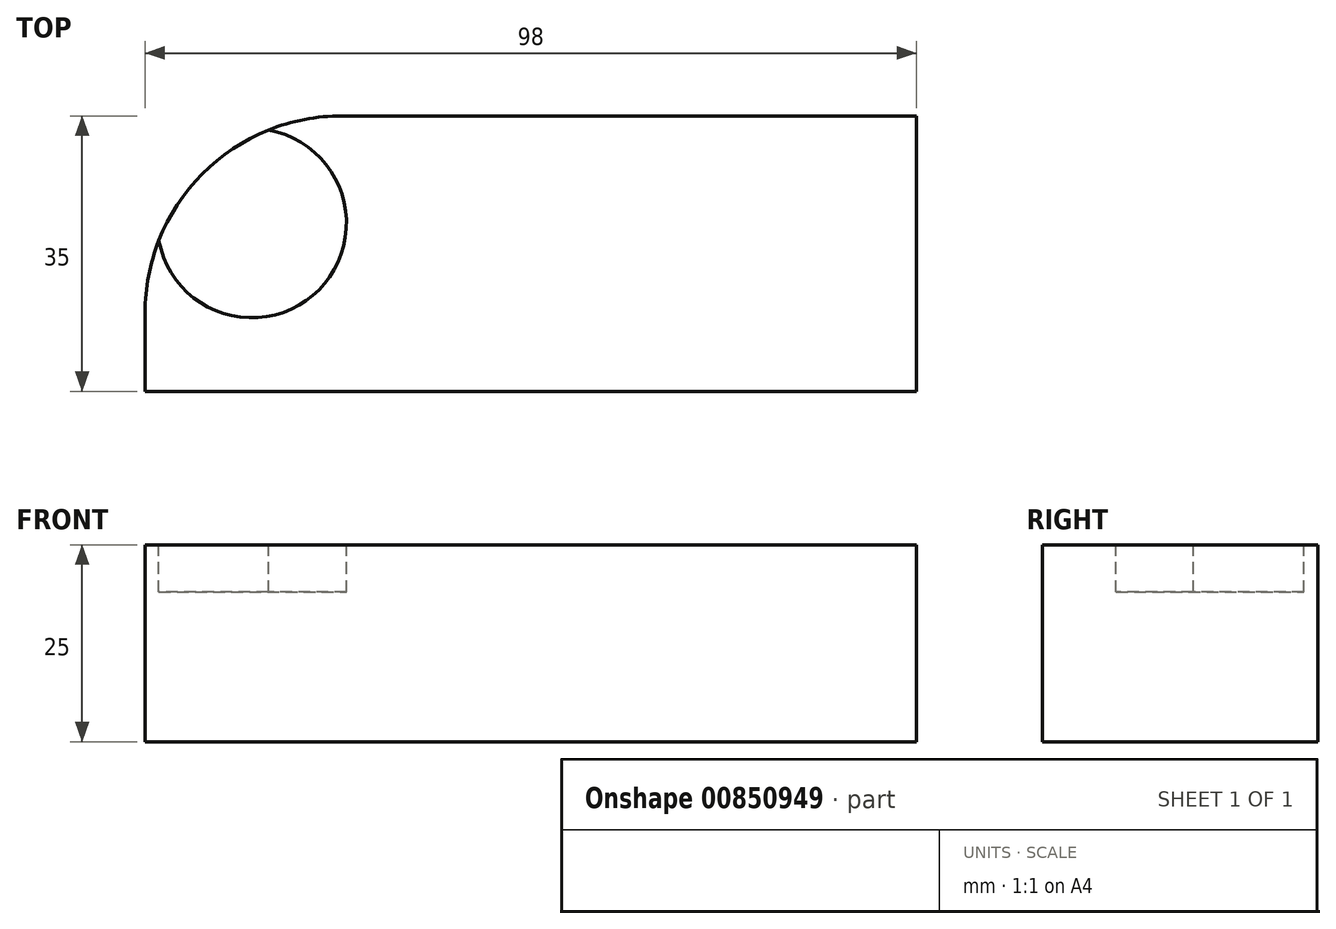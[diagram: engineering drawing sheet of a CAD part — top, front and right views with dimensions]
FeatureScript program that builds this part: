
annotation { "Feature Type Name" : "Feature", "Feature Type Description" : "" }
export const myFeature = defineFeature(function(context is Context, id is Id, definition is map)
    precondition{}
    {
        {
            var Q0;
            Q0=qCreatedBy(makeId("Top.planeOp"),FACE);
            var sketch = newSketch(context, id + "F0", { "sketchPlane" : qUnion([Q0])});
            skLineSegment(sketch, "E0.bottom", {"start": v(-8.8, 41.17) * mm, "end": v(64.2, 41.17) * mm});
            skLineSegment(sketch, "E0.top", {"start": v(-33.8, 6.17) * mm, "end": v(64.2, 6.17) * mm});
            skLineSegment(sketch, "E0.left", {"start": v(-33.8, 16.17) * mm, "end": v(-33.8, 6.17) * mm});
            skLineSegment(sketch, "E0.right", {"start": v(64.2, 41.17) * mm, "end": v(64.2, 6.17) * mm});
            skPoint(sketch, "E1.visualSharp", {"position": v(-33.8, 41.17) * mm});
            skArc(sketch, "E1.filletArc", {"start": v(-8.8, 41.17) * mm, "mid": v(-26.47, 33.85) * mm, "end": v(-33.8, 16.17) * mm});
            skSolve(sketch);
        }
        {
            var Q0;
            Q0=makeQuery(id+"F0.imprint","IMPRINT",FACE,{"disambiguationData":[TD([[makeQuery(id+"F0.imprint","IMPRINT",EDGE,{"derivedFrom":sQuery(id+"F0.wireOp",EDGE,"E0.bottom")}),-1.0]])]});
            extrude(context, id + "F1", {"entities" : qUnion([Q0]), "depth" : 25 * mm, "offsetDistance" : 25 * mm});
        }
        {
            var Q0;
            Q0=makeQuery(id+"F1.opExtrude","CAP_FACE",FACE,{"disambiguationData":[OSD([sQuery(id+"F0.wireOp",EDGE,"E0.bottom"),sQuery(id+"F0.wireOp",EDGE,"E0.top"),sQuery(id+"F0.wireOp",EDGE,"E0.left"),sQuery(id+"F0.wireOp",EDGE,"E0.right")])],"isStart":false});
            var sketch = newSketch(context, id + "F2", { "sketchPlane" : qUnion([Q0])});
            skCircle(sketch, "E2", {"center": v(-20.24, 27.53) * mm, "radius": 12.01 * mm});
            skSolve(sketch);
        }
        {
            var Q0;
            Q0=makeQuery(id+"F2.imprint","IMPRINT",FACE,{"disambiguationData":[TD([[makeQuery(id+"F2.imprint","IMPRINT",EDGE,{"derivedFrom":sQuery(id+"F2.wireOp",EDGE,"E2")}),1.0]])]});
            var Q1;
            Q1=sQuery(id+"F2.wireOp",EDGE,"E2");
            extrude(context, id + "F3", {"entities" : qUnion([Q0]), "operationType" : NewBodyOperationType.REMOVE, "surfaceEntities" : qUnion([Q1]), "oppositeDirection" : true, "depth" : 6 * mm, "offsetDistance" : 25 * mm});
        }
    });
